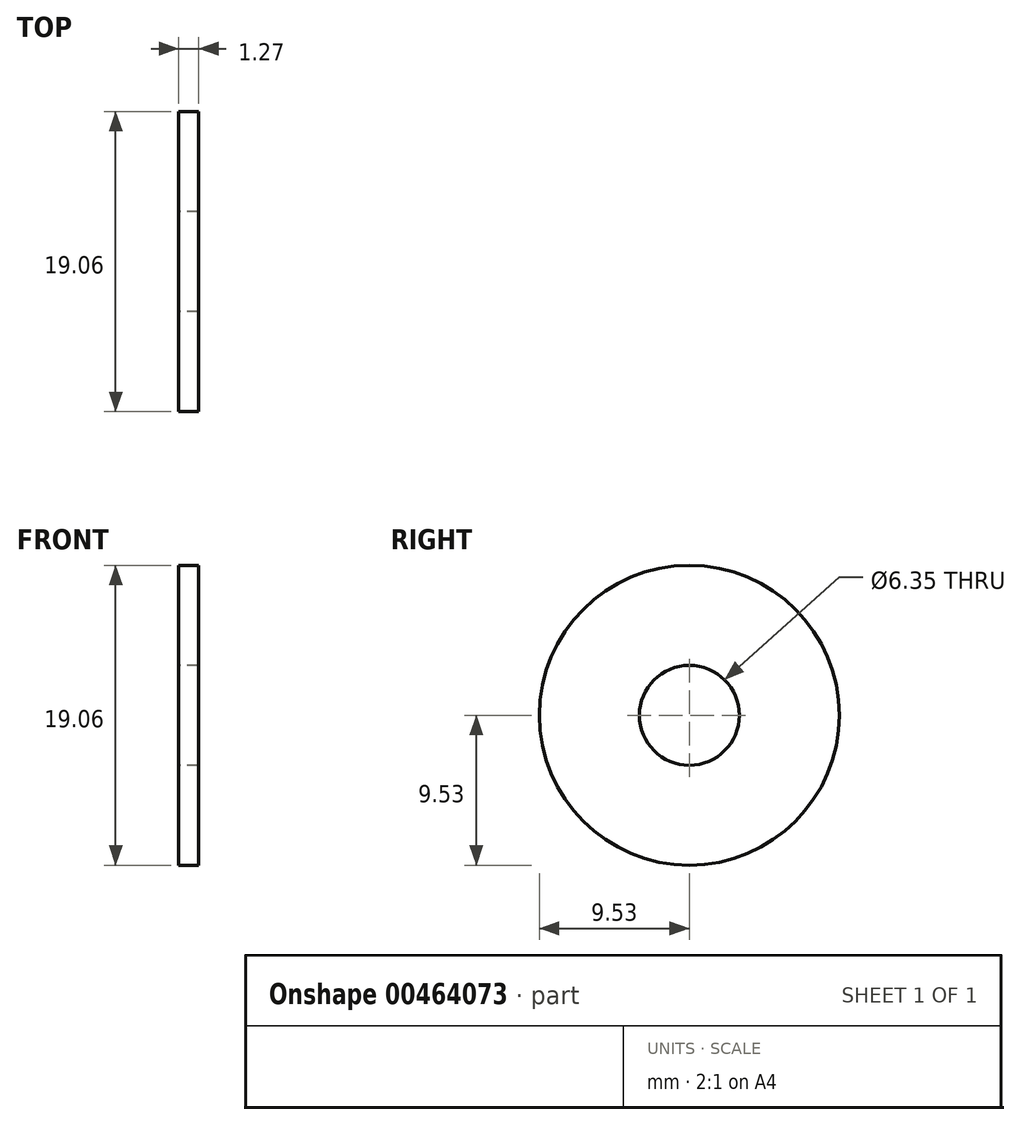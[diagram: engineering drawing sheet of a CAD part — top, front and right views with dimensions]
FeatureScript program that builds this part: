
annotation { "Feature Type Name" : "Feature", "Feature Type Description" : "" }
export const myFeature = defineFeature(function(context is Context, id is Id, definition is map)
    precondition{}
    {
        {
            var Q0;
            Q0=qCreatedBy(makeId("Right.planeOp"),FACE);
            var sketch = newSketch(context, id + "F0", { "sketchPlane" : qUnion([Q0])});
            skCircle(sketch, "E0", {"center": v(0, 0) * mm, "radius": 9.53 * mm});
            skCircle(sketch, "E1", {"center": v(0, 0) * mm, "radius": 3.18 * mm});
            skSolve(sketch);
        }
        {
            var Q0;
            Q0=makeQuery(id+"F0.imprint","IMPRINT",FACE,{"disambiguationData":[TD([[makeQuery(id+"F0.imprint","IMPRINT",EDGE,{"derivedFrom":sQuery(id+"F0.wireOp",EDGE,"E0")}),1.0]])]});
            extrude(context, id + "F1", {"entities" : qUnion([Q0]), "depth" : 1.27 * mm, "offsetDistance" : 25.4 * mm});
        }
    });
